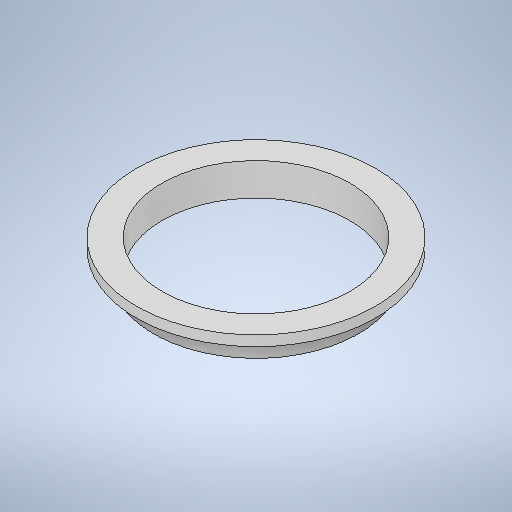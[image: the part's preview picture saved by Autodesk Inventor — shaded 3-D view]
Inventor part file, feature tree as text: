
AUTODESK INVENTOR PART (.ipt)
format: ipt  version: 2025.1 (Build 291241000, 241)  size: 263,680 bytes
history: native  units: mm
features: sketch x2, revolve x1, hole x1
ambient origin geometry x8: Origin, YZ Plane, XZ Plane, XY Plane, X Axis, Y Axis, Z Axis, Center Point
bodies: Solid1 (feature_tree)
feature tree (4):
  revolve  "Revolution1"  [1 undecoded]
  hole  "Hole1"  [1 undecoded]
  sketch  "Sketch1"  dims[d0=700.0mm d1=600.0mm]
  sketch  "Sketch2"  dims[d3=65.0mm d4=90.0deg d5=550.0mm d6=6.0mm d7=4.0mm d8=2.0mm d9=90.0deg d10=8.0mm d11=20.594885mm d12=30.0mm]
note: 2 required parameter values undecoded (feature->parameter linkage not recoverable at this tier; creation-order binding heuristic only, values carry confidence <= 0.55)